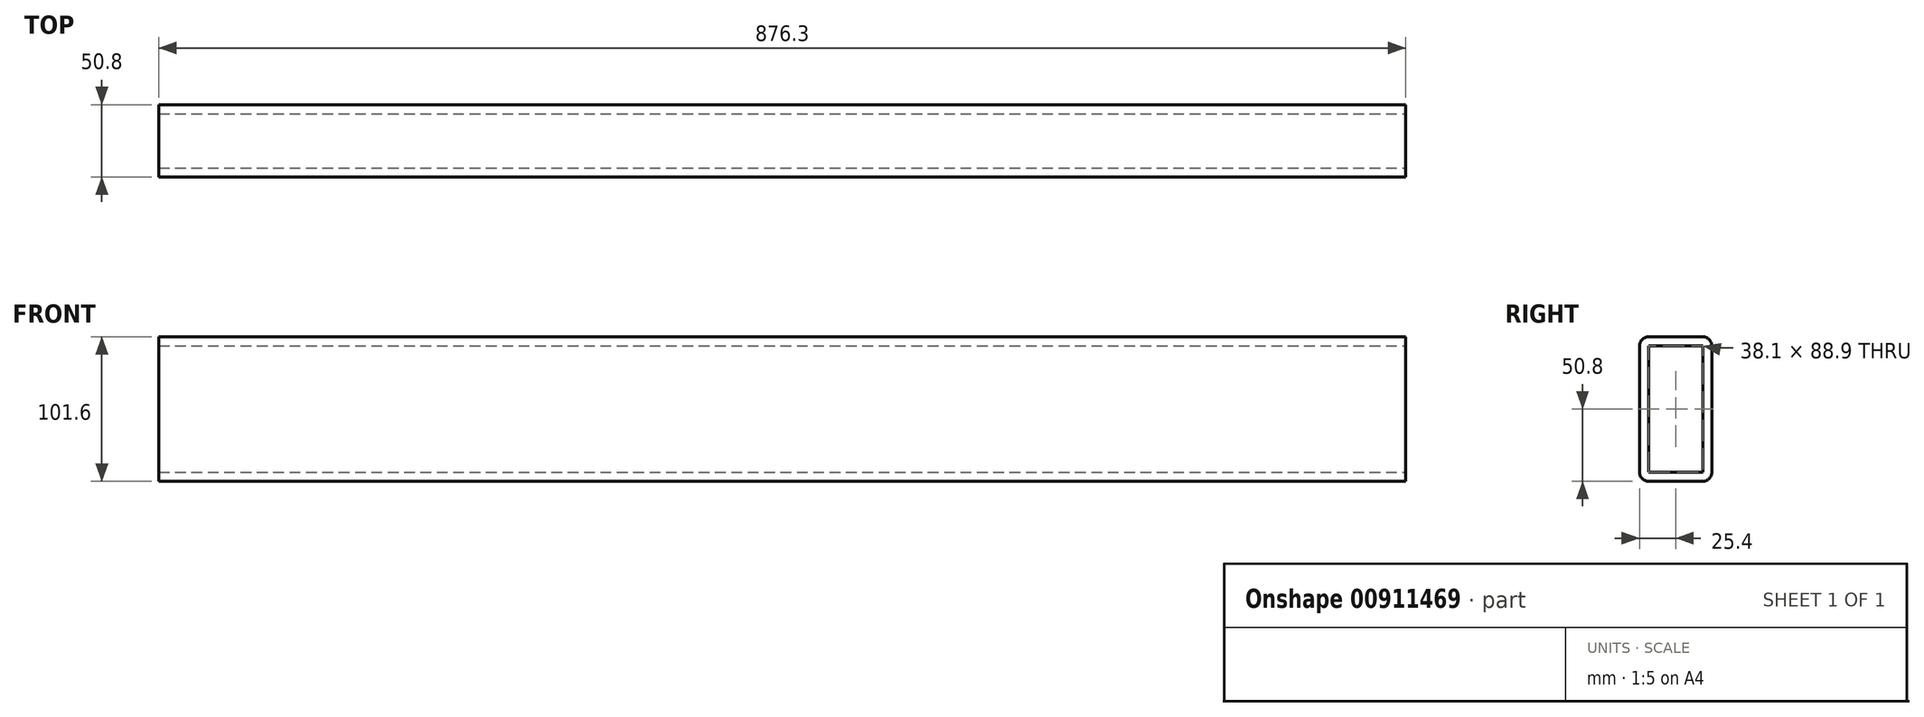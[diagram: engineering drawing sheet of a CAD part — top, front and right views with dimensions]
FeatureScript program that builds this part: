
annotation { "Feature Type Name" : "Feature", "Feature Type Description" : "" }
export const myFeature = defineFeature(function(context is Context, id is Id, definition is map)
    precondition{}
    {
        {
            var Q0;
            Q0=qCreatedBy(makeId("Right.planeOp"),FACE);
            var sketch = newSketch(context, id + "F0", { "sketchPlane" : qUnion([Q0])});
            skLineSegment(sketch, "E0.bottom", {"start": v(19.05, 50.8) * mm, "end": v(-19.05, 50.8) * mm});
            skLineSegment(sketch, "E0.top", {"start": v(19.05, -50.8) * mm, "end": v(-19.05, -50.8) * mm});
            skLineSegment(sketch, "E0.left", {"start": v(25.4, 44.45) * mm, "end": v(25.4, -44.45) * mm});
            skLineSegment(sketch, "E0.right", {"start": v(-25.4, 44.45) * mm, "end": v(-25.4, -44.45) * mm});
            skPoint(sketch, "E0.middle", {"position": v(0, 0) * mm});
            skPoint(sketch, "E1.visualSharp", {"position": v(-25.4, 50.8) * mm});
            skArc(sketch, "E1.filletArc", {"start": v(-19.05, 50.8) * mm, "mid": v(-23.54, 48.94) * mm, "end": v(-25.4, 44.45) * mm});
            skPoint(sketch, "E2.visualSharp", {"position": v(-25.4, -50.8) * mm});
            skArc(sketch, "E2.filletArc", {"start": v(-25.4, -44.45) * mm, "mid": v(-23.54, -48.94) * mm, "end": v(-19.05, -50.8) * mm});
            skPoint(sketch, "E3.visualSharp", {"position": v(25.4, -50.8) * mm});
            skArc(sketch, "E3.filletArc", {"start": v(19.05, -50.8) * mm, "mid": v(23.54, -48.94) * mm, "end": v(25.4, -44.45) * mm});
            skPoint(sketch, "E4.visualSharp", {"position": v(25.4, 50.8) * mm});
            skArc(sketch, "E4.filletArc", {"start": v(25.4, 44.45) * mm, "mid": v(23.54, 48.94) * mm, "end": v(19.05, 50.8) * mm});
            skLineSegment(sketch, "E5.0", {"start": v(-19.05, 44.45) * mm, "end": v(-19.05, -44.45) * mm});
            skLineSegment(sketch, "E5.1", {"start": v(19.05, 44.45) * mm, "end": v(-19.05, 44.45) * mm});
            skLineSegment(sketch, "E5.2", {"start": v(19.05, 44.45) * mm, "end": v(19.05, -44.45) * mm});
            skLineSegment(sketch, "E5.3", {"start": v(19.05, -44.45) * mm, "end": v(-19.05, -44.45) * mm});
            skSolve(sketch);
        }
        {
            var Q0;
            Q0=makeQuery(id+"F0.imprint","IMPRINT",FACE,{"disambiguationData":[TD([[makeQuery(id+"F0.imprint","IMPRINT",EDGE,{"derivedFrom":sQuery(id+"F0.wireOp",EDGE,"E0.bottom")}),1.0]])]});
            extrude(context, id + "F1", {"entities" : qUnion([Q0]), "oppositeDirection" : true, "depth" : 876.3 * mm, "offsetDistance" : 25.4 * mm});
        }
    });
